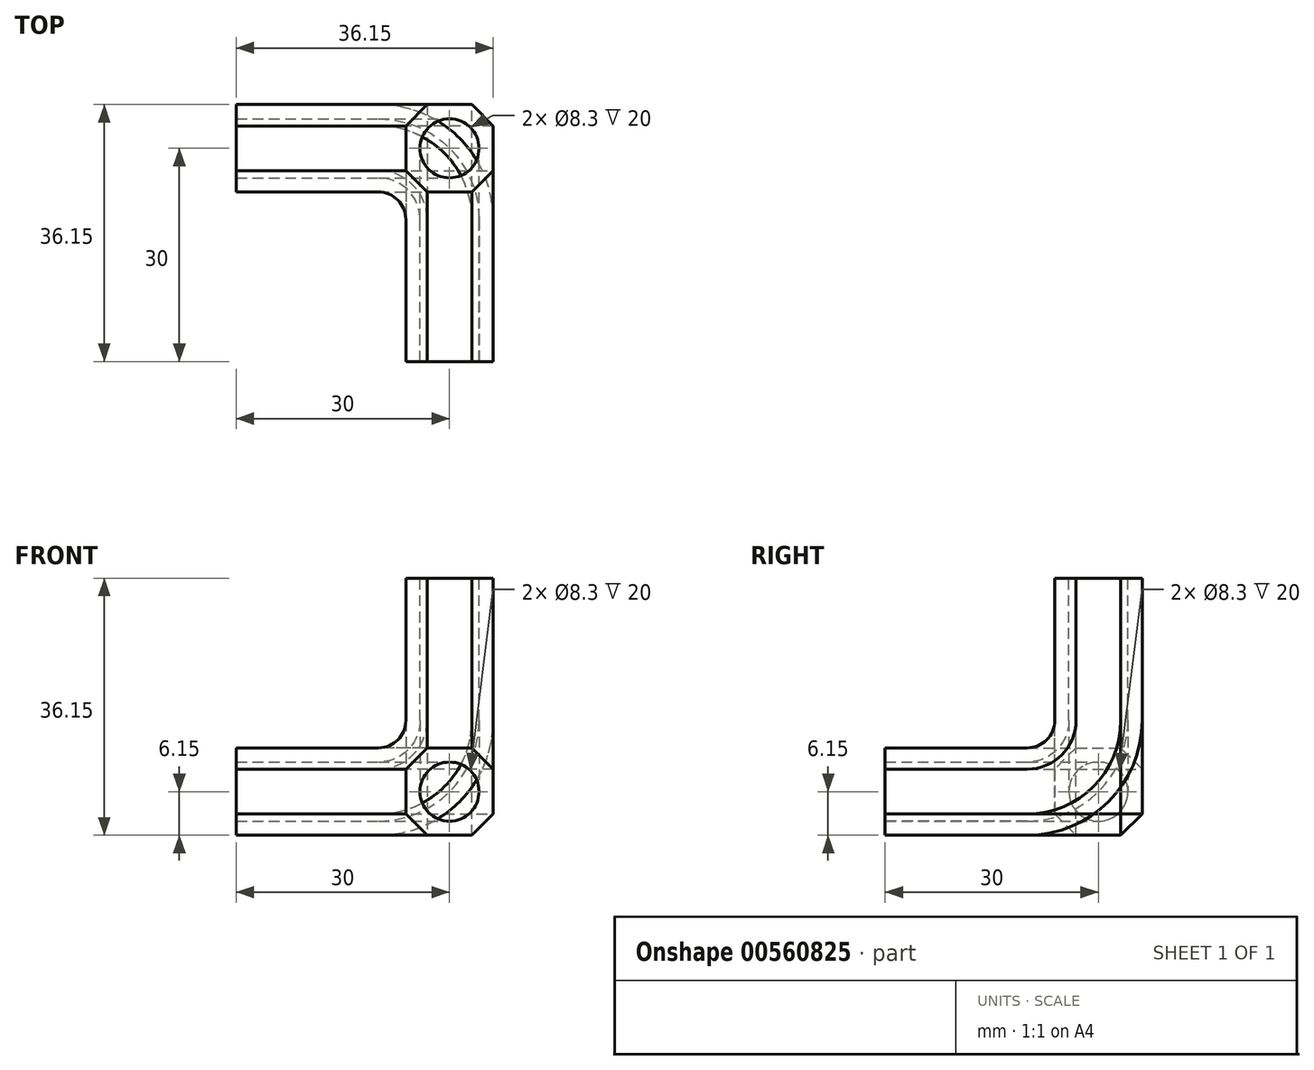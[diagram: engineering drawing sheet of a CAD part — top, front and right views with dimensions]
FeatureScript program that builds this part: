
annotation { "Feature Type Name" : "Feature", "Feature Type Description" : "" }
export const myFeature = defineFeature(function(context is Context, id is Id, definition is map)
    precondition{}
    {
        {
            var Q0;
            Q0=qCreatedBy(makeId("Front.planeOp"),FACE);
            var sketch = newSketch(context, id + "F0", { "sketchPlane" : qUnion([Q0])});
            skLineSegment(sketch, "E0", {"start": v(0, 0) * mm, "end": v(20, 0) * mm});
            skLineSegment(sketch, "E1", {"start": v(30, 10) * mm, "end": v(30, 30) * mm});
            skPoint(sketch, "E2.visualSharp", {"position": v(30, 0) * mm});
            skArc(sketch, "E2.filletArc", {"start": v(20, 0) * mm, "mid": v(27.07, 2.93) * mm, "end": v(30, 10) * mm});
            skSolve(sketch);
        }
        {
            var Q0;
            Q0=qCreatedBy(makeId("Right.planeOp"),FACE);
            var sketch = newSketch(context, id + "F1", { "sketchPlane" : qUnion([Q0])});
            skCircle(sketch, "E3", {"center": v(0, 0) * mm, "radius": 4.15 * mm});
            skCircle(sketch, "E4", {"center": v(0, 0) * mm, "radius": 6.15 * mm, "construction": true});
            skLineSegment(sketch, "E5.bottom", {"start": v(-6.15, 6.15) * mm, "end": v(6.15, 6.15) * mm});
            skLineSegment(sketch, "E5.top", {"start": v(-6.15, -6.15) * mm, "end": v(6.15, -6.15) * mm});
            skLineSegment(sketch, "E5.left", {"start": v(-6.15, 6.15) * mm, "end": v(-6.15, -6.15) * mm});
            skLineSegment(sketch, "E5.right", {"start": v(6.15, 6.15) * mm, "end": v(6.15, -6.15) * mm});
            skSolve(sketch);
        }
        {
            var Q0;
            Q0=makeQuery(id+"F1.imprint","IMPRINT",FACE,{"disambiguationData":[TD([[makeQuery(id+"F1.imprint","IMPRINT",EDGE,{"derivedFrom":sQuery(id+"F1.wireOp",EDGE,"E3")}),-1.0]])]});
            var Q1;
            Q1=sQuery(id+"F0.wireOp",EDGE,"E0");
            var Q2;
            Q2=sQuery(id+"F0.wireOp",EDGE,"E2.filletArc");
            var Q3;
            Q3=sQuery(id+"F0.wireOp",EDGE,"E1");
            sweep(context, id + "F2", {"profiles" : qUnion([Q0]), "path" : qUnion([Q1, Q2, Q3])});
        }
        {
            var Q0;
            Q0=makeQuery(id+"F2.opSweep","SWEPT_EDGE",EDGE,{"disambiguationData":[OSD([sQuery(id+"F0.wireOp",EDGE,"E1"),sQuery(id+"F1.wireOp",EDGE,"E5.bottom"),sQuery(id+"F1.wireOp",EDGE,"E5.left")])]});
            var Q1;
            Q1=makeQuery(id+"F2.opSweep","SWEPT_EDGE",EDGE,{"disambiguationData":[OSD([sQuery(id+"F0.wireOp",EDGE,"E1"),sQuery(id+"F1.wireOp",EDGE,"E5.top"),sQuery(id+"F1.wireOp",EDGE,"E5.left")])]});
            var Q2;
            Q2=makeQuery(id+"F2.opSweep","SWEPT_EDGE",EDGE,{"disambiguationData":[OSD([sQuery(id+"F0.wireOp",EDGE,"E1"),sQuery(id+"F1.wireOp",EDGE,"E5.top"),sQuery(id+"F1.wireOp",EDGE,"E5.right")])]});
            var Q3;
            Q3=makeQuery(id+"F2.opSweep","SWEPT_EDGE",EDGE,{"disambiguationData":[OSD([sQuery(id+"F0.wireOp",EDGE,"E1"),sQuery(id+"F1.wireOp",EDGE,"E5.bottom"),sQuery(id+"F1.wireOp",EDGE,"E5.right")])]});
            var Q4;
            Q4=makeQuery(id+"F2.opSweep","SWEPT_EDGE",EDGE,{"disambiguationData":[OSD([sQuery(id+"F0.wireOp",EDGE,"E0"),sQuery(id+"F1.wireOp",EDGE,"E5.top"),sQuery(id+"F1.wireOp",EDGE,"E5.left")])]});
            var Q5;
            Q5=makeQuery(id+"F72un8gFeBFyOCp_1.opExtrude","SWEPT_EDGE",EDGE,{"disambiguationData":[OSD([sQuery(id+"FfZI6mcZtl9lH79_1.wireOp",EDGE,"VuCL6RYj-EHlV-t7rd-TVDf-kKCsCcFAymia.top"),sQuery(id+"FfZI6mcZtl9lH79_1.wireOp",EDGE,"VuCL6RYj-EHlV-t7rd-TVDf-kKCsCcFAymia.left")])]});
            var Q6;
            Q6=makeQuery(id+"F72un8gFeBFyOCp_1.opExtrude","SWEPT_EDGE",EDGE,{"disambiguationData":[OSD([sQuery(id+"FfZI6mcZtl9lH79_1.wireOp",EDGE,"VuCL6RYj-EHlV-t7rd-TVDf-kKCsCcFAymia.bottom"),sQuery(id+"FfZI6mcZtl9lH79_1.wireOp",EDGE,"VuCL6RYj-EHlV-t7rd-TVDf-kKCsCcFAymia.right")])]});
            var Q7;
            Q7=makeQuery(id+"F72un8gFeBFyOCp_1.opExtrude","SWEPT_EDGE",EDGE,{"disambiguationData":[OSD([sQuery(id+"F0.wireOp",EDGE,"E2.filletArc"),sQuery(id+"F1.wireOp",EDGE,"E5.bottom"),sQuery(id+"F1.wireOp",EDGE,"E5.left"),sQuery(id+"FfZI6mcZtl9lH79_1.wireOp",EDGE,"VuCL6RYj-EHlV-t7rd-TVDf-kKCsCcFAymia.left"),sQuery(id+"FfZI6mcZtl9lH79_1.wireOp",EDGE,"ad429725-937d-4178-a744-5d7371b68342.0")])]});
            chamfer(context, id + "F3", {"entities" : qUnion([Q0, Q1, Q2, Q3, Q4, Q5, Q6, Q7]), "width" : 3 * mm, "tangentPropagation" : true});
        }
        {
            var Q0;
            Q0=makeQuery(id+"F2.opSweep","SWEPT_BODY",BODY,{"disambiguationData":[OSD([sQuery(id+"F0.wireOp",EDGE,"E1"),sQuery(id+"F1.wireOp",EDGE,"E3"),sQuery(id+"F1.wireOp",EDGE,"E5.bottom"),sQuery(id+"F1.wireOp",EDGE,"E5.top"),sQuery(id+"F1.wireOp",EDGE,"E5.left"),sQuery(id+"F1.wireOp",EDGE,"E5.right")])]});
            var Q1;
            Q1=makeQuery(id+"F2.opSweep","SWEPT_FACE",FACE,{"disambiguationData":[OSD([sQuery(id+"F0.wireOp",EDGE,"E1"),sQuery(id+"F1.wireOp",EDGE,"E3")])]});
            circularPattern(context, id + "F4", {"entities" : qUnion([Q0]), "axis" : qUnion([Q1]), "angle" : 90 * degree, "instanceCount" : 2, "oppositeDirection" : true});
        }
        {
            var Q0;
            Q0=makeQuery(id+"F2.opSweep","SWEPT_BODY",BODY,{"disambiguationData":[OSD([sQuery(id+"F0.wireOp",EDGE,"E1"),sQuery(id+"F1.wireOp",EDGE,"E3"),sQuery(id+"F1.wireOp",EDGE,"E5.bottom"),sQuery(id+"F1.wireOp",EDGE,"E5.top"),sQuery(id+"F1.wireOp",EDGE,"E5.left"),sQuery(id+"F1.wireOp",EDGE,"E5.right")])]});
            var Q1;
            Q1=makeQuery(id+"F2.opSweep","SWEPT_FACE",FACE,{"disambiguationData":[OSD([sQuery(id+"F0.wireOp",EDGE,"E0"),sQuery(id+"F1.wireOp",EDGE,"E3")])]});
            circularPattern(context, id + "F5", {"entities" : qUnion([Q0]), "axis" : qUnion([Q1]), "angle" : 90 * degree, "instanceCount" : 2, "oppositeDirection" : true});
        }
    });
